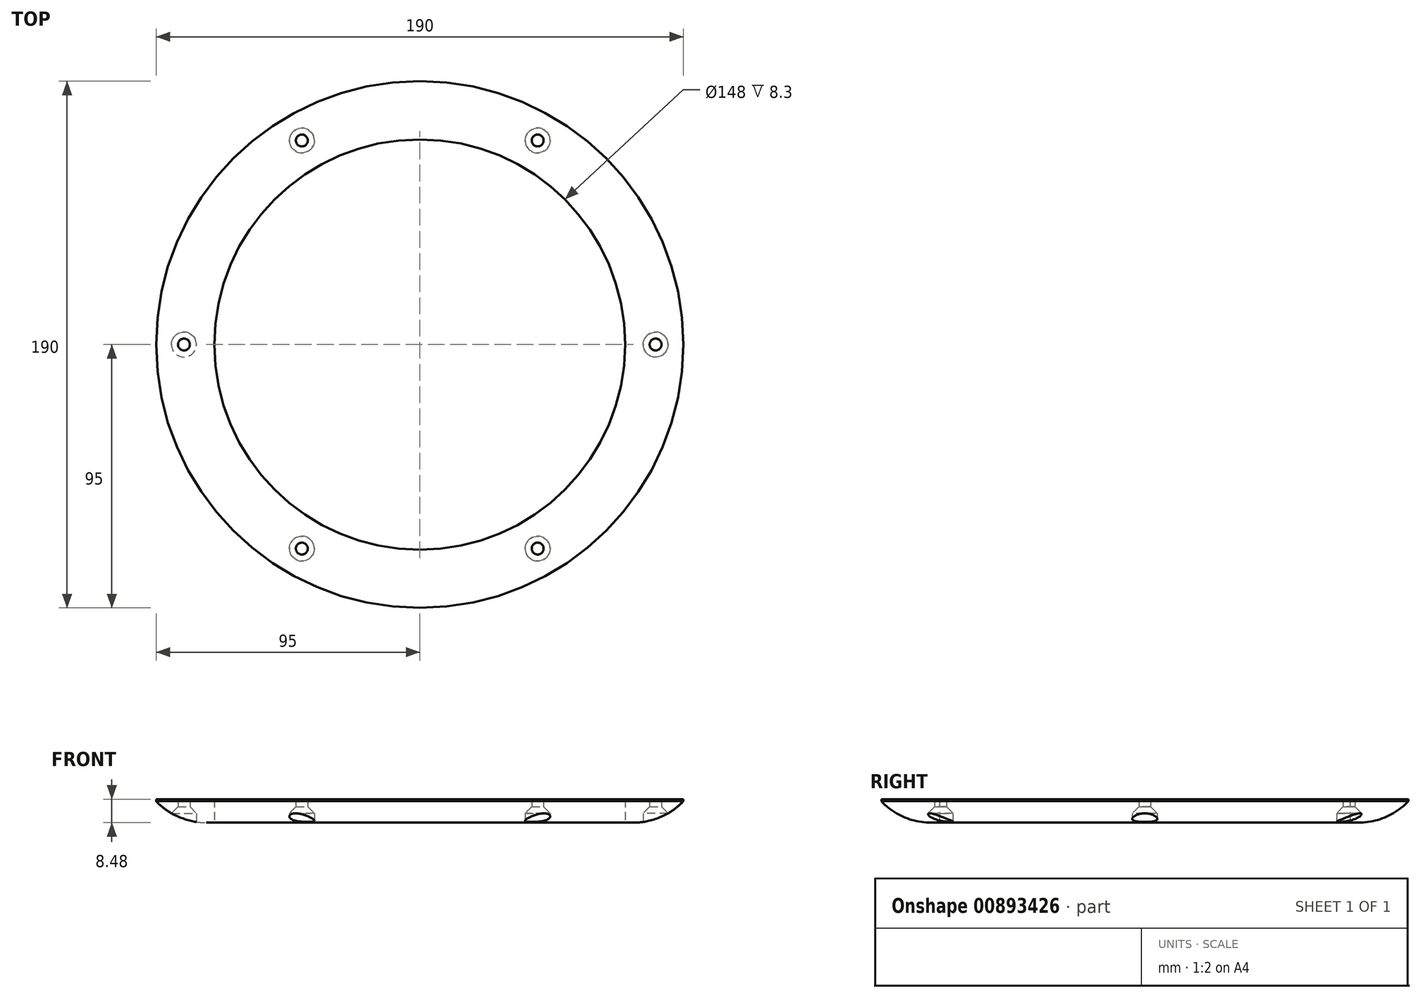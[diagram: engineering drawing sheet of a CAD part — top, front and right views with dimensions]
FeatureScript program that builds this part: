
annotation { "Feature Type Name" : "Feature", "Feature Type Description" : "" }
export const myFeature = defineFeature(function(context is Context, id is Id, definition is map)
    precondition{}
    {
        {
            var Q0;
            Q0=qCreatedBy(makeId("Front.planeOp"),FACE);
            var sketch = newSketch(context, id + "F0", { "sketchPlane" : qUnion([Q0])});
            skLineSegment(sketch, "E0", {"start": v(-95, 7.56) * mm, "end": v(-95, 8.3) * mm});
            skLineSegment(sketch, "E1", {"start": v(-95, 8.3) * mm, "end": v(-74, 8.3) * mm});
            skPoint(sketch, "E2.orphan", {"position": v(0, 2.08) * mm});
            skArc(sketch, "E3", {"start": v(-95, 7.56) * mm, "mid": v(-85.4, 1.29) * mm, "end": v(-74, 0) * mm});
            skPoint(sketch, "E4.orphan", {"position": v(-95, 0) * mm});
            skLineSegment(sketch, "E5", {"start": v(0, -3.52) * mm, "end": v(0, 22.4) * mm});
            skLineSegment(sketch, "E6", {"start": v(-74, 0) * mm, "end": v(-74, 8.3) * mm});
            skSolve(sketch);
        }
        {
            var Q0;
            Q0 = qSketchRegion(id + "F0", true);
            var Q1;
            Q1=sQuery(id+"F0.wireOp",EDGE,"E5");
            revolve(context, id + "F1", {"surfaceOperationType" : NewSurfaceOperationType.NEW, "entities" : qUnion([Q0]), "axis" : qUnion([Q1]), "revolveType" : RevolveType.FULL});
        }
        {
            var Q0;
            Q0=makeQuery(id+"F1.opRevolve","SWEPT_FACE",FACE,{"disambiguationData":[OSD([sQuery(id+"F0.wireOp",EDGE,"E1")])]});
            cPlane(context, id + "F2", {"entities" : qUnion([Q0]), "cplaneType" : CPlaneType.OFFSET, "offset" : 11 * mm, "oppositeDirection" : true, "width" : 150 * mm, "height" : 150 * mm});
        }
        {
            var Q0;
            Q0=qCreatedBy(id+"F2.planeOp",FACE);
            var sketch = newSketch(context, id + "F3", { "sketchPlane" : qUnion([Q0])});
            skPoint(sketch, "E7", {"position": v(-85, 0) * mm});
            skPoint(sketch, "E8.start.orphan", {"position": v(0, 0) * mm});
            skPoint(sketch, "E9.1.0", {"position": v(-42.5, -73.61) * mm});
            skPoint(sketch, "E9.2.0", {"position": v(42.5, -73.61) * mm});
            skPoint(sketch, "E10.0.3.0", {"position": v(85, 0) * mm});
            skPoint(sketch, "E10.0.4.0", {"position": v(42.5, 73.61) * mm});
            skPoint(sketch, "E10.0.5.0", {"position": v(-42.5, 73.61) * mm});
            skSolve(sketch);
        }
        {
            var Q0;
            Q0=sQuery(id+"F3.wireOp",VERTEX,"E7");
            var Q1;
            Q1=sQuery(id+"F3.wireOp",VERTEX,"E9.1.0");
            var Q2;
            Q2=sQuery(id+"F3.wireOp",VERTEX,"E9.2.0");
            var Q3;
            Q3=sQuery(id+"F3.wireOp",VERTEX,"E10.0.3.0");
            var Q4;
            Q4=sQuery(id+"F3.wireOp",VERTEX,"E10.0.4.0");
            var Q5;
            Q5=sQuery(id+"F3.wireOp",VERTEX,"E10.0.5.0");
            var Q6;
            Q6=makeQuery(id+"F1.opRevolve","SWEPT_BODY",BODY,{"disambiguationData":[OSD([sQuery(id+"F0.wireOp",EDGE,"E0"),sQuery(id+"F0.wireOp",EDGE,"E1"),sQuery(id+"F0.wireOp",EDGE,"E3"),sQuery(id+"F0.wireOp",EDGE,"E6")])]});
            hole(context, id + "F4", {"style" : HoleStyle.C_SINK, "endStyle" : HoleEndStyle.BLIND, "oppositeDirection" : true, "holeDiameter" : 4.3 * mm, "cSinkDiameter" : 9 * mm, "cSinkAngle" : 90 * degree, "majorDiameter" : 5 * mm, "holeDepth" : 15 * mm, "isTappedThrough" : true, "tappedDepth" : 12 * mm, "tapClearance" : 3, "locations" : qUnion([Q0, Q1, Q2, Q3, Q4, Q5]), "scope" : qUnion([Q6])});
        }
    });
